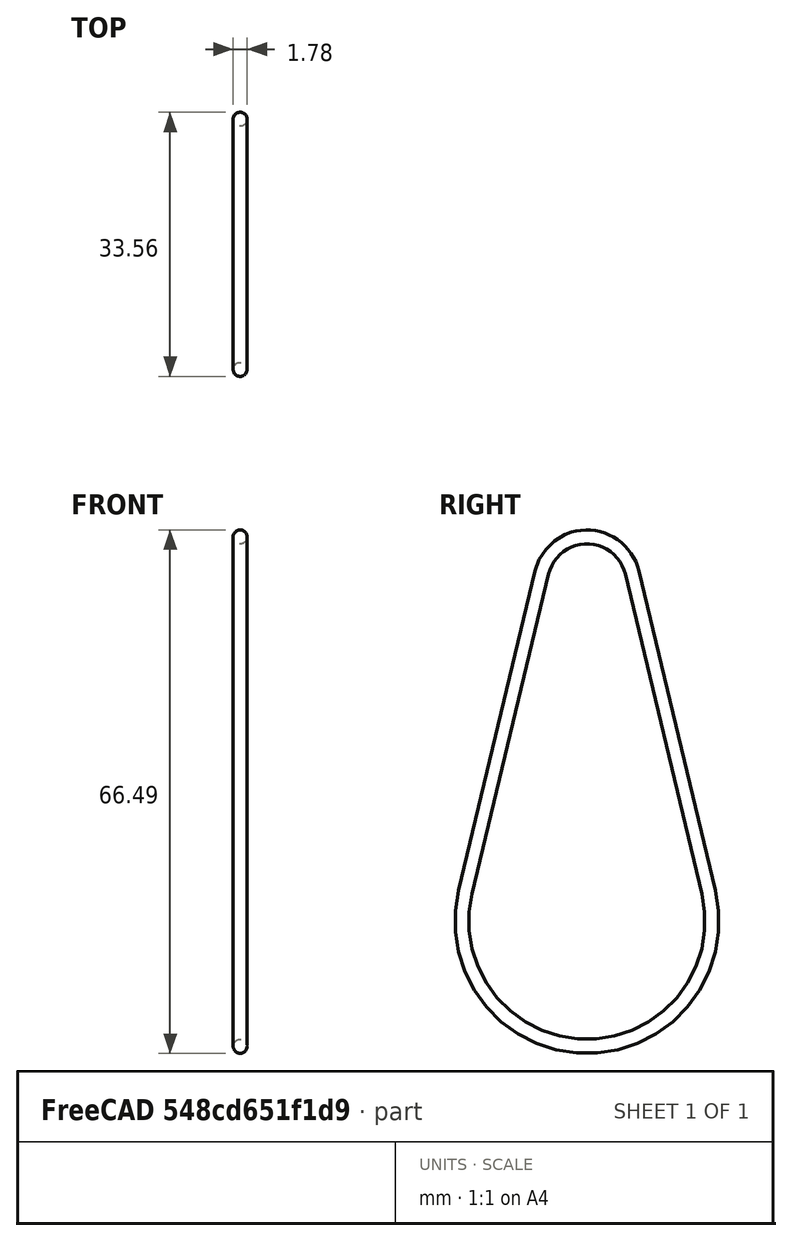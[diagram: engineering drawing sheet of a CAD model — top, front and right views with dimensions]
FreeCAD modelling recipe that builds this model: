
FCSTD DOCUMENT  (FreeCAD 0.18.4R)
Label: quimera_encoder_o-ring
License: All rights reserved
LicenseURL: http://en.wikipedia.org/wiki/All_rights_reserved
objects: Sketcher::SketchObject×2, PartDesign::AdditivePipe×1, PartDesign::Body×1
note: 5 computed .brp shape members not serialized (recipe doc carries the construction recipe); baked Part::Feature solids carry a one-line shape summary decoded from their .brp

FEATURE [Sketcher::SketchObject] Sketch
  MapMode = 5
  Placement = pos=(0,0,0) rot=(0.57735,0.57735,0.57735;2.0944rad)
  Support = -> [YZ_Plane]
  sketch-geometry (6):
    g0: Circle [constr] CenterX=0 CenterY=0 CenterZ=0 NormalX=0 NormalY=0 NormalZ=1 AngleXU=0 Radius=5
    g1: Circle [constr] CenterX=0 CenterY=-42.93 CenterZ=0 NormalX=0 NormalY=0 NormalZ=1 AngleXU=0 Radius=15
    g2: ArcOfCircle CenterX=0 CenterY=0 CenterZ=0 NormalX=0 NormalY=0 NormalZ=1 AngleXU=0 Radius=5.89 StartAngle=0.235097 EndAngle=2.9065
    g3: ArcOfCircle CenterX=0 CenterY=-42.93 CenterZ=0 NormalX=0 NormalY=0 NormalZ=1 AngleXU=0 Radius=15.89 StartAngle=2.9065 EndAngle=6.51828
    g4: LineSegment StartX=-15.4529 StartY=-39.2286 StartZ=0 EndX=-5.72798 EndY=1.372 EndZ=0
    g5: LineSegment StartX=15.4529 StartY=-39.2286 StartZ=0 EndX=5.72798 EndY=1.372 EndZ=0
  constraints (13):
    c: Coincident(g0,g-1)
    c: Vertical(g1,g0)
    c: DistanceY(g1) = -42.93
    c: Radius(g1) = 15
    c: Radius(g0) = 5
    c: Coincident(g2,g-1)
    c: Coincident(g3,g1)
    c: Radius(g2) = 5.89
    c: Radius(g3) = 15.89
    c: Tangent(g5,g3) = -1.5708
    c: Tangent(g4,g3) = 1.5708
    c: Tangent(g4,g2) = 1.5708
    c: Tangent(g5,g2) = -1.5708
FEATURE [Sketcher::SketchObject] Sketch001
  MapMode = 5
  Placement = pos=(0,0,0) rot=(1,0,0;1.5708rad)
  Support = -> [XZ_Plane]
  sketch-geometry (1):
    g0: Circle CenterX=0 CenterY=5.89 CenterZ=0 NormalX=0 NormalY=0 NormalZ=1 AngleXU=0 Radius=0.89
  constraints (3):
    c: PointOnObject(g0,g-2)
    c: Radius(g0) = 0.89
    c: DistanceY(g0) = 5.89
FEATURE [PartDesign::AdditivePipe] AdditivePipe
  AuxilleryCurvelinear = true
  AuxillerySpineTangent = false
  Binormal = (0,0,0)
  Mode = 0
  Placement = pos=(0,0,0) rot=(1,0,0;1.5708rad)
  Profile = -> Sketch001
  Spine = -> Sketch
  SpineTangent = false
  Transformation = 0
  Transition = 0
FEATURE [PartDesign::Body] Body
  Group = -> [Sketch,Sketch001,AdditivePipe]
  Origin = -> Origin
  Tip = -> AdditivePipe
